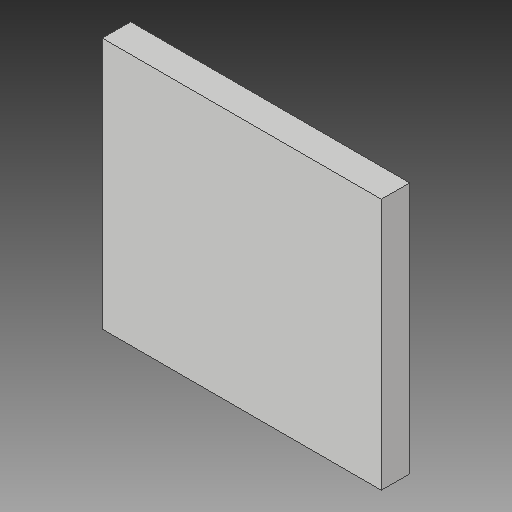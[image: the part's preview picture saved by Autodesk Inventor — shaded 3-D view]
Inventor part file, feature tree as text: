
AUTODESK INVENTOR PART (.ipt)
format: ipt  version: 2018 (Build 220112000, 112)  size: 79,872 bytes
history: native  units: mm
features: extrude x1, sketch x1
ambient origin geometry x8: Origin, YZ Plane, XZ Plane, XY Plane, X Axis, Y Axis, Z Axis, Center Point
bodies: Body1 (feature_tree)
feature tree (2):
  extrude  "Extrusão2"  Depth=125.0mm
  sketch  "Esboço2"  dims[d3=112.9mm d4=125.0mm d5=12.7mm d6=0.0mm]
